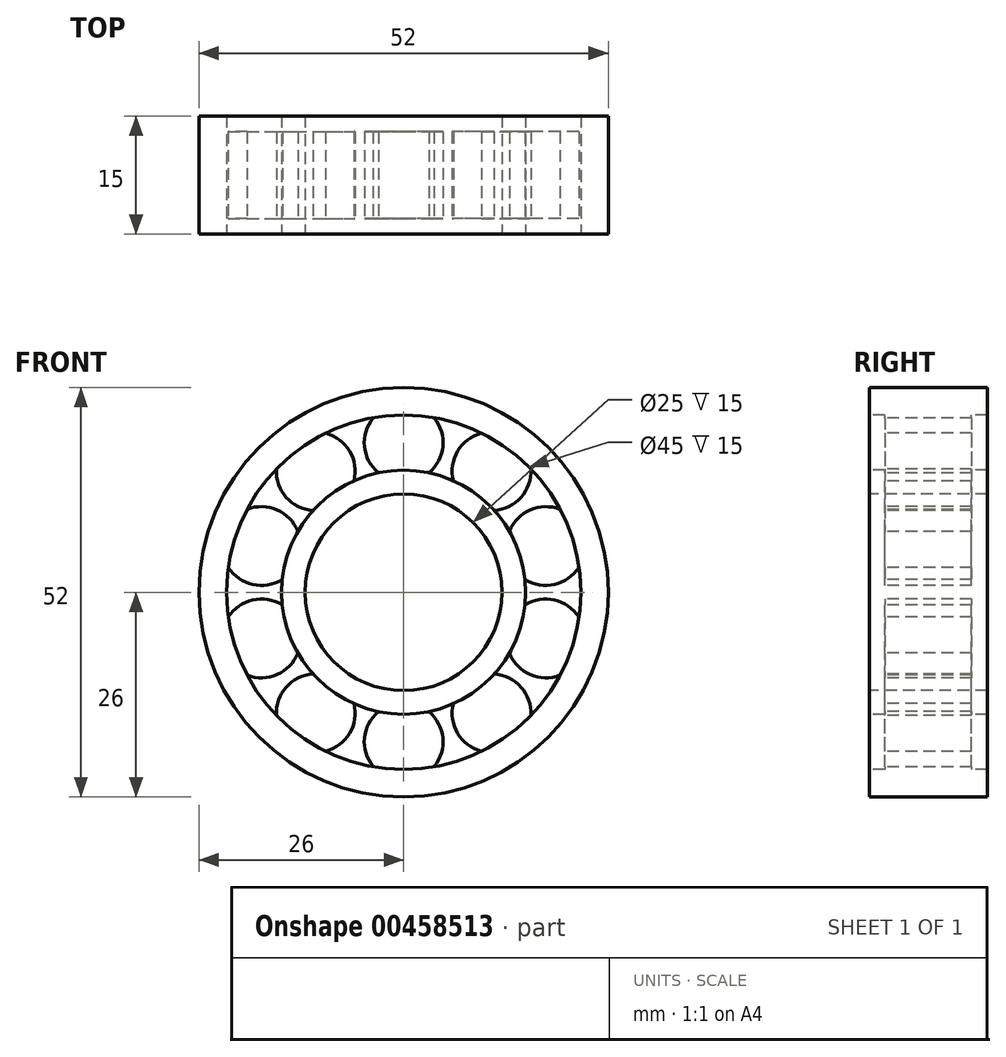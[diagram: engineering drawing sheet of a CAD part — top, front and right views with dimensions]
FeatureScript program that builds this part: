
annotation { "Feature Type Name" : "Feature", "Feature Type Description" : "" }
export const myFeature = defineFeature(function(context is Context, id is Id, definition is map)
    precondition{}
    {
        {
            var Q0;
            Q0=qCreatedBy(makeId("Front.planeOp"),FACE);
            var sketch = newSketch(context, id + "F0", { "sketchPlane" : qUnion([Q0])});
            skCircle(sketch, "E0", {"center": v(0, 0) * mm, "radius": 12.5 * mm});
            skCircle(sketch, "E1", {"center": v(0, 0) * mm, "radius": 15.5 * mm});
            skCircle(sketch, "E2", {"center": v(0, 0) * mm, "radius": 22.5 * mm});
            skCircle(sketch, "E3", {"center": v(0, 0) * mm, "radius": 26 * mm});
            skSolve(sketch);
        }
        {
            var Q0;
            Q0=makeQuery(id+"F0.imprint","IMPRINT",FACE,{"disambiguationData":[TD([[makeQuery(id+"F0.imprint","IMPRINT",EDGE,{"derivedFrom":sQuery(id+"F0.wireOp",EDGE,"E0")}),-1.0]])]});
            extrude(context, id + "F1", {"entities" : qUnion([Q0]), "oppositeDirection" : true, "depth" : 15 * mm});
        }
        {
            var Q0;
            Q0=makeQuery(id+"F0.imprint","IMPRINT",FACE,{"disambiguationData":[TD([[makeQuery(id+"F0.imprint","IMPRINT",EDGE,{"derivedFrom":sQuery(id+"F0.wireOp",EDGE,"E2")}),-1.0]])]});
            extrude(context, id + "F2", {"entities" : qUnion([Q0]), "oppositeDirection" : true, "depth" : 15 * mm});
        }
        {
            var Q0;
            Q0=qCreatedBy(makeId("Front.planeOp"),FACE);
            cPlane(context, id + "F3", {"entities" : qUnion([Q0]), "cplaneType" : CPlaneType.OFFSET, "offset" : 2 * mm, "oppositeDirection" : true, "width" : 150 * mm, "height" : 150 * mm});
        }
        {
            var Q0;
            Q0=qCreatedBy(id+"F3.planeOp",FACE);
            var sketch = newSketch(context, id + "F4", { "sketchPlane" : qUnion([Q0])});
            skCircle(sketch, "E4", {"center": v(0, 19) * mm, "radius": 5 * mm});
            skSolve(sketch);
        }
        {
            var Q0;
            Q0 = qSketchRegion(id + "F4", true);
            extrude(context, id + "F5", {"entities" : qUnion([Q0]), "oppositeDirection" : true, "depth" : 11 * mm});
        }
        {
            var Q0;
            Q0=makeQuery(id+"F5.opExtrude","SWEPT_BODY",BODY,{"disambiguationData":[OSD([sQuery(id+"F4.wireOp",EDGE,"E4")])]});
            var Q1;
            Q1=sQuery(id+"F0.wireOp",EDGE,"E0");
            circularPattern(context, id + "F6", {"operationType" : NewBodyOperationType.ADD, "entities" : qUnion([Q0]), "axis" : qUnion([Q1]), "angle" : 360 * degree, "instanceCount" : 10, "equalSpace" : true, "isCentered" : true});
        }
    });
